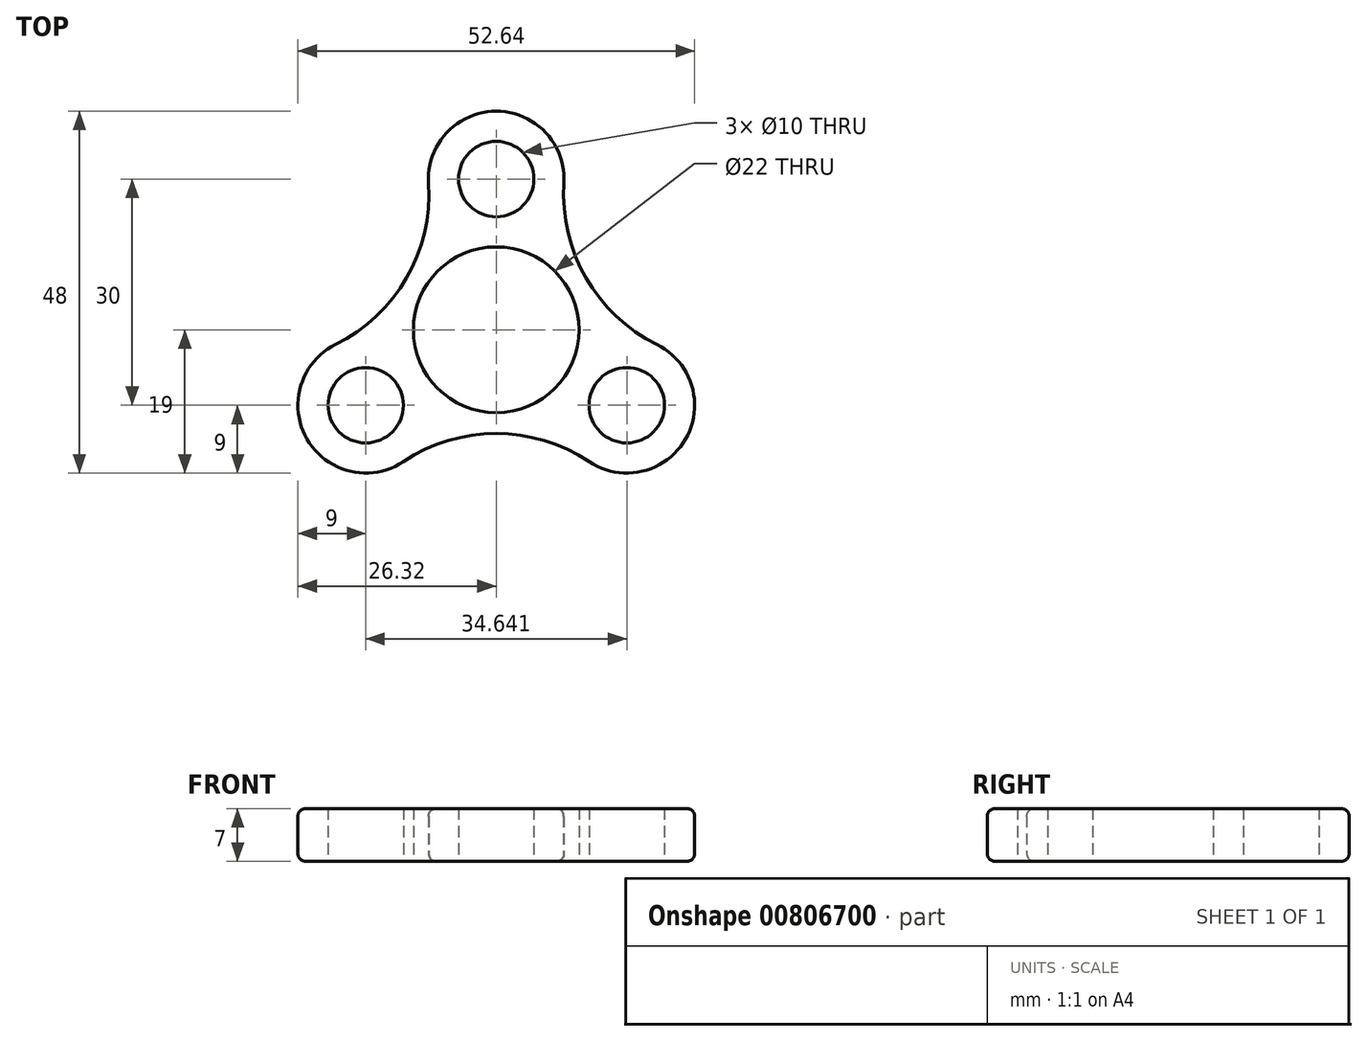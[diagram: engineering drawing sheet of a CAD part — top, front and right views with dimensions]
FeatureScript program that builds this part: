
annotation { "Feature Type Name" : "Feature", "Feature Type Description" : "" }
export const myFeature = defineFeature(function(context is Context, id is Id, definition is map)
    precondition{}
    {
        {
            var Q0;
            Q0=qCreatedBy(makeId("Top.planeOp"),FACE);
            var sketch = newSketch(context, id + "F0", { "sketchPlane" : qUnion([Q0])});
            skCircle(sketch, "E0", {"center": v(0, 0) * mm, "radius": 11 * mm});
            skCircle(sketch, "E1", {"center": v(0, 20) * mm, "radius": 5 * mm});
            skLineSegment(sketch, "E2", {"start": v(0, 0) * mm, "end": v(184.83, 106.71) * mm, "construction": true});
            skLineSegment(sketch, "E3", {"start": v(0, 0) * mm, "end": v(152.8, -88.22) * mm, "construction": true});
            skLineSegment(sketch, "E4", {"start": v(0, 0) * mm, "end": v(-211.29, -121.99) * mm, "construction": true});
            skLineSegment(sketch, "E5", {"start": v(0, 0) * mm, "end": v(-209.5, 120.95) * mm, "construction": true});
            skCircle(sketch, "E6", {"center": v(31.18, 18) * mm, "radius": 22.24 * mm});
            skCircle(sketch, "E7", {"center": v(17.32, -10) * mm, "radius": 5 * mm});
            skCircle(sketch, "E8", {"center": v(0, -36) * mm, "radius": 22.24 * mm});
            skCircle(sketch, "E9", {"center": v(-17.32, -10) * mm, "radius": 5 * mm});
            skCircle(sketch, "E10", {"center": v(-31.18, 18) * mm, "radius": 22.24 * mm});
            skCircle(sketch, "E11", {"center": v(0, 20) * mm, "radius": 9 * mm});
            skCircle(sketch, "E12", {"center": v(17.32, -10) * mm, "radius": 9 * mm});
            skCircle(sketch, "E13", {"center": v(-17.32, -10) * mm, "radius": 9 * mm});
            skSolve(sketch);
        }
        {
            var Q0;
            Q0=makeQuery(id+"F0.imprint","IMPRINT",FACE,{"disambiguationData":[TD([[makeQuery(id+"F0.imprint","IMPRINT",EDGE,{"derivedFrom":sQuery(id+"F0.wireOp",EDGE,"E7")}),-1.0]])]});
            var Q1;
            Q1=makeQuery(id+"F0.imprint","IMPRINT",FACE,{"disambiguationData":[TD([[makeQuery(id+"F0.imprint","IMPRINT",EDGE,{"derivedFrom":sQuery(id+"F0.wireOp",EDGE,"E9")}),-1.0]])]});
            var Q2;
            Q2=makeQuery(id+"F0.imprint","IMPRINT",FACE,{"disambiguationData":[TD([[makeQuery(id+"F0.imprint","IMPRINT",EDGE,{"derivedFrom":sQuery(id+"F0.wireOp",EDGE,"E0")}),-1.0]])]});
            var Q3;
            Q3=makeQuery(id+"F0.imprint","IMPRINT",FACE,{"disambiguationData":[TD([[makeQuery(id+"F0.imprint","IMPRINT",EDGE,{"derivedFrom":sQuery(id+"F0.wireOp",EDGE,"E1")}),-1.0]])]});
            extrude(context, id + "F1", {"entities" : qUnion([Q0, Q1, Q2, Q3]), "depth" : 7 * mm, "offsetDistance" : 25 * mm});
        }
        {
            var Q0;
            Q0=makeQuery(id+"F1.opExtrude","CAP_EDGE",EDGE,{"disambiguationData":[OSD([sQuery(id+"F0.wireOp",EDGE,"E13")])],"isStart":false});
            var Q1;
            Q1=makeQuery(id+"F1.opExtrude","CAP_EDGE",EDGE,{"disambiguationData":[OSD([sQuery(id+"F0.wireOp",EDGE,"E8")])],"isStart":false});
            var Q2;
            Q2=makeQuery(id+"F1.opExtrude","CAP_EDGE",EDGE,{"disambiguationData":[OSD([sQuery(id+"F0.wireOp",EDGE,"E12")])],"isStart":false});
            var Q3;
            Q3=makeQuery(id+"F1.opExtrude","CAP_EDGE",EDGE,{"disambiguationData":[OSD([sQuery(id+"F0.wireOp",EDGE,"E6")])],"isStart":false});
            var Q4;
            Q4=makeQuery(id+"F1.opExtrude","CAP_EDGE",EDGE,{"disambiguationData":[OSD([sQuery(id+"F0.wireOp",EDGE,"E10")])],"isStart":false});
            var Q5;
            Q5=makeQuery(id+"F1.opExtrude","CAP_EDGE",EDGE,{"disambiguationData":[OSD([sQuery(id+"F0.wireOp",EDGE,"E11")])],"isStart":false});
            var Q6;
            Q6=makeQuery(id+"F1.opExtrude","CAP_EDGE",EDGE,{"disambiguationData":[OSD([sQuery(id+"F0.wireOp",EDGE,"E12")])],"isStart":true});
            var Q7;
            Q7=makeQuery(id+"F1.opExtrude","CAP_EDGE",EDGE,{"disambiguationData":[OSD([sQuery(id+"F0.wireOp",EDGE,"E8")])],"isStart":true});
            var Q8;
            Q8=makeQuery(id+"F1.opExtrude","CAP_EDGE",EDGE,{"disambiguationData":[OSD([sQuery(id+"F0.wireOp",EDGE,"E13")])],"isStart":true});
            var Q9;
            Q9=makeQuery(id+"F1.opExtrude","CAP_EDGE",EDGE,{"disambiguationData":[OSD([sQuery(id+"F0.wireOp",EDGE,"E10")])],"isStart":true});
            var Q10;
            Q10=makeQuery(id+"F1.opExtrude","CAP_EDGE",EDGE,{"disambiguationData":[OSD([sQuery(id+"F0.wireOp",EDGE,"E11")])],"isStart":true});
            var Q11;
            Q11=makeQuery(id+"F1.opExtrude","CAP_EDGE",EDGE,{"disambiguationData":[OSD([sQuery(id+"F0.wireOp",EDGE,"E6")])],"isStart":true});
            fillet(context, id + "F2", {"entities" : qUnion([Q0, Q1, Q2, Q3, Q4, Q5, Q6, Q7, Q8, Q9, Q10, Q11]), "tangentPropagation" : true, "radius" : 1 * mm, "defaultsChanged" : false, "vertexSettings" : [], "allowEdgeOverflow" : false});
        }
    });
